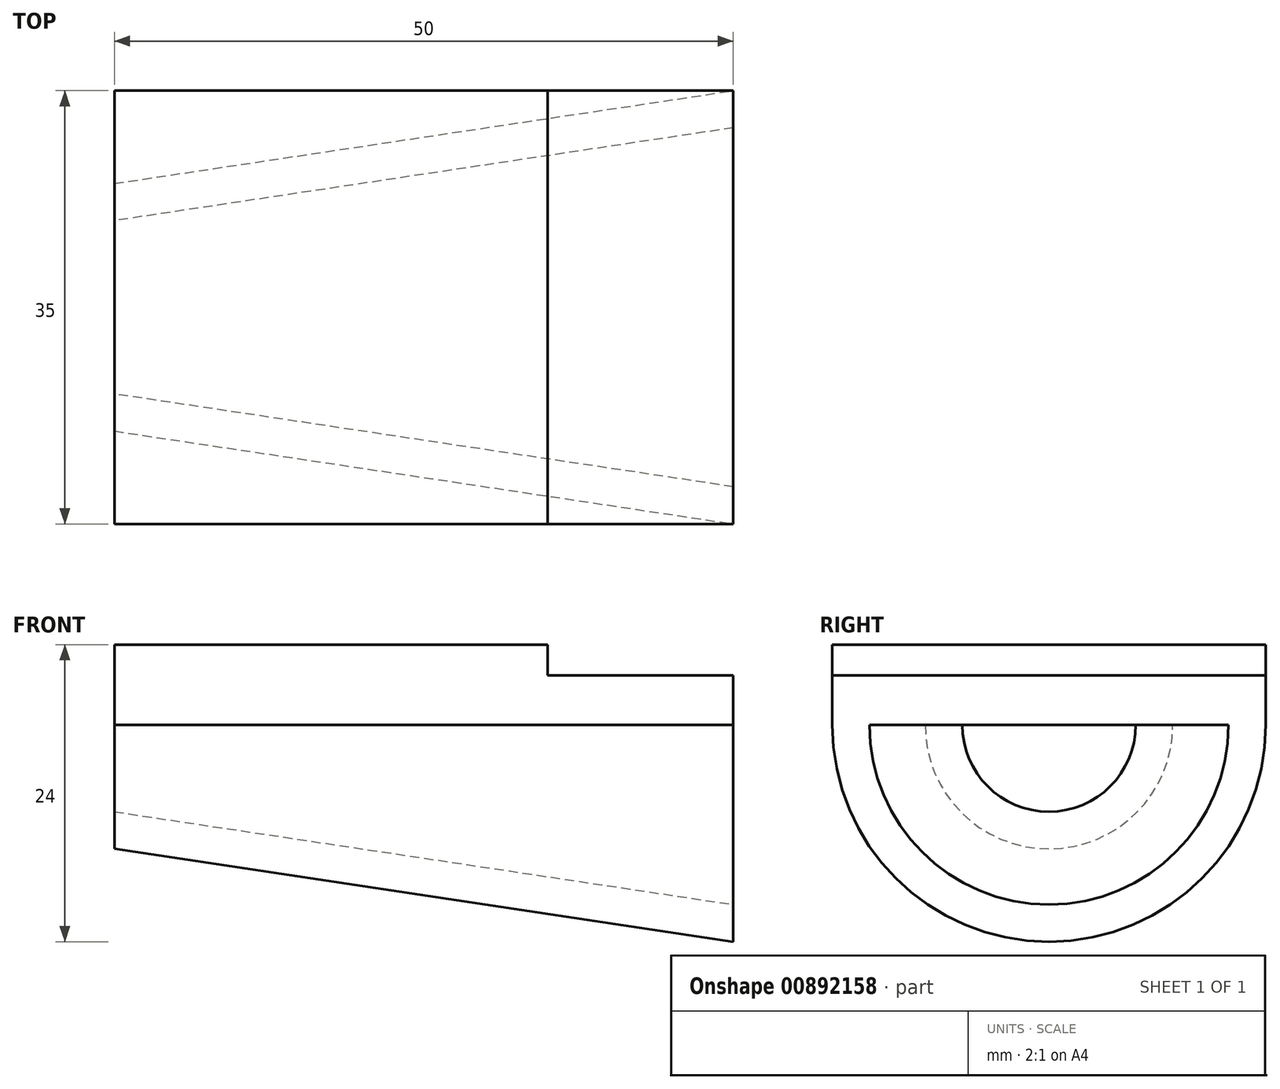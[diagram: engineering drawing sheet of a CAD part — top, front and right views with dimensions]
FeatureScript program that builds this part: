
annotation { "Feature Type Name" : "Feature", "Feature Type Description" : "" }
export const myFeature = defineFeature(function(context is Context, id is Id, definition is map)
    precondition{}
    {
        {
            var Q0;
            Q0=qCreatedBy(makeId("Front.planeOp"),FACE);
            var sketch = newSketch(context, id + "F0", { "sketchPlane" : qUnion([Q0])});
            skLineSegment(sketch, "E0", {"start": v(0, 0) * mm, "end": v(-15, 0) * mm});
            skLineSegment(sketch, "E1", {"start": v(-15, 0) * mm, "end": v(-15, 2.5) * mm});
            skLineSegment(sketch, "E2", {"start": v(-15, 2.5) * mm, "end": v(-50, 2.5) * mm});
            skLineSegment(sketch, "E3", {"start": v(0, -4) * mm, "end": v(0, 0) * mm});
            skLineSegment(sketch, "E4", {"start": v(-50, 2.5) * mm, "end": v(-50, -4) * mm});
            skLineSegment(sketch, "E5", {"start": v(-50, -4) * mm, "end": v(0, -4) * mm});
            skSolve(sketch);
        }
        {
            var Q0;
            Q0=makeQuery(id+"F0.imprint","IMPRINT",FACE,{"disambiguationData":[TD([[makeQuery(id+"F0.imprint","IMPRINT",EDGE,{"derivedFrom":sQuery(id+"F0.wireOp",EDGE,"E0")}),1.0]])]});
            extrude(context, id + "F1", {"entities" : qUnion([Q0]), "depth" : 35 * mm, "offsetDistance" : 25 * mm});
        }
        {
            var Q0;
            Q0=makeQuery(id+"F1.opExtrude","SWEPT_FACE",FACE,{"disambiguationData":[OSD([sQuery(id+"F0.wireOp",EDGE,"E5")])]});
            var sketch = newSketch(context, id + "F2", { "sketchPlane" : qUnion([Q0])});
            skLineSegment(sketch, "E6", {"start": v(0, 0) * mm, "end": v(0, 3) * mm});
            skLineSegment(sketch, "E7", {"start": v(0, 3) * mm, "end": v(-50, 10.5) * mm});
            skLineSegment(sketch, "E8", {"start": v(-50, 10.5) * mm, "end": v(-50, 7.5) * mm});
            skLineSegment(sketch, "E9", {"start": v(-50, 7.5) * mm, "end": v(0, 0) * mm});
            skLineSegment(sketch, "E10", {"start": v(-58.97, 17.5) * mm, "end": v(1.29, 17.5) * mm});
            skSolve(sketch);
        }
        {
            var Q0;
            Q0=makeQuery(id+"F2.imprint","IMPRINT",FACE,{"disambiguationData":[TD([[makeQuery(id+"F2.imprint","IMPRINT",EDGE,{"derivedFrom":sQuery(id+"F2.wireOp",EDGE,"E6")}),-1.0]])]});
            var Q1;
            Q1=sQuery(id+"F2.wireOp",EDGE,"E10");
            revolve(context, id + "F3", {"operationType" : NewBodyOperationType.ADD, "surfaceOperationType" : NewSurfaceOperationType.NEW, "entities" : qUnion([Q0]), "axis" : qUnion([Q1]), "revolveType" : RevolveType.ONE_DIRECTION, "oppositeDirection" : true, "angle" : 180 * degree});
        }
    });
